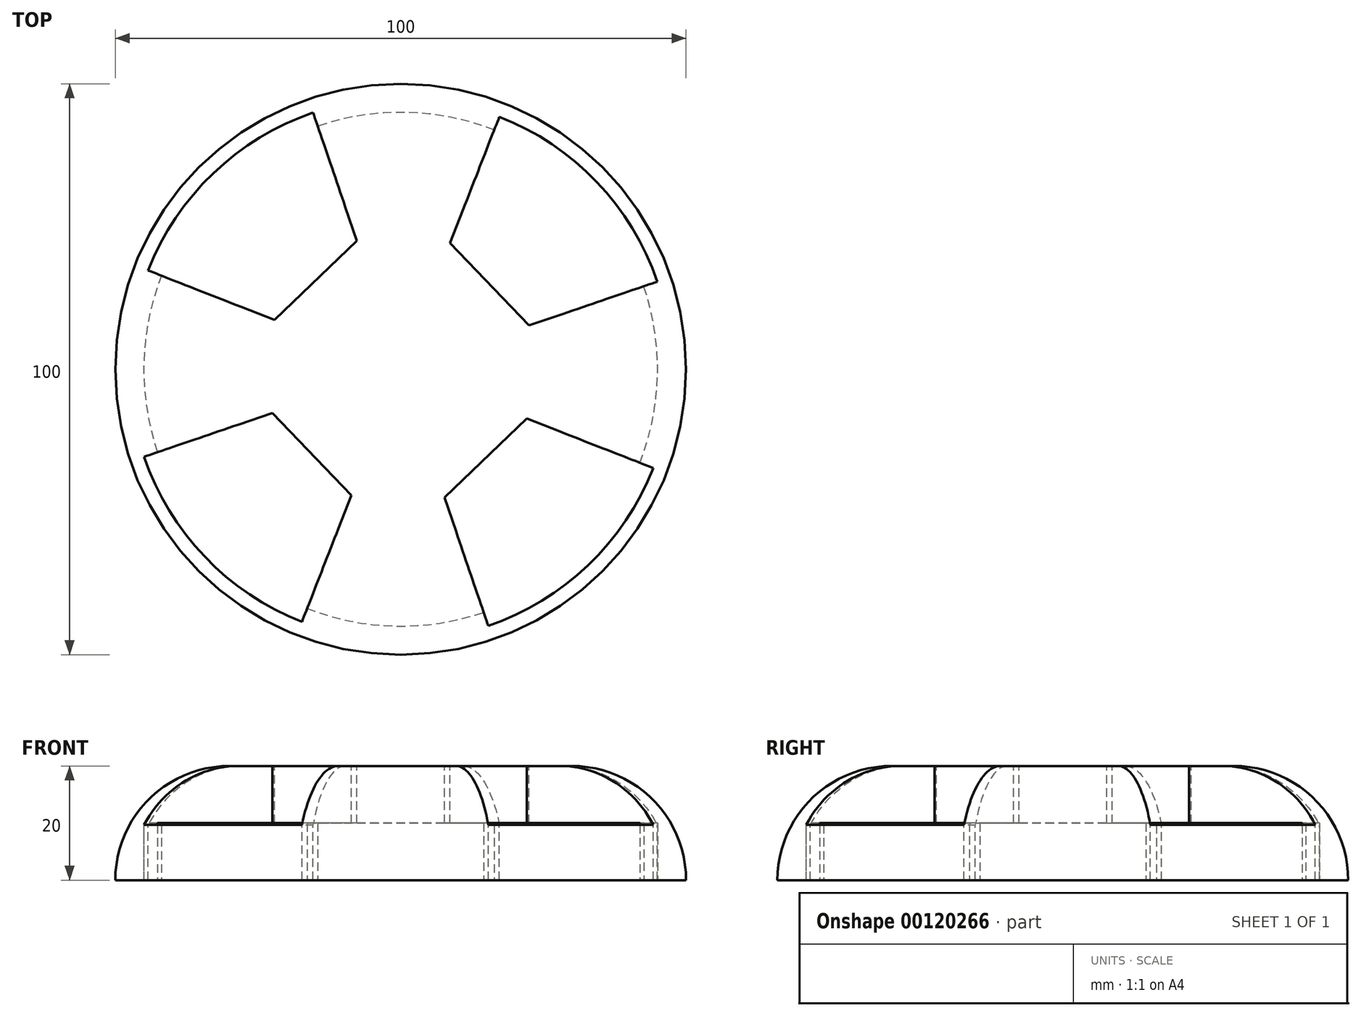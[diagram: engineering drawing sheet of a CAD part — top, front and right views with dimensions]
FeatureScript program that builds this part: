
annotation { "Feature Type Name" : "Feature", "Feature Type Description" : "" }
export const myFeature = defineFeature(function(context is Context, id is Id, definition is map)
    precondition{}
    {
        {
            var Q0;
            Q0=qCreatedBy(makeId("Top.planeOp"),FACE);
            var sketch = newSketch(context, id + "F0", { "sketchPlane" : qUnion([Q0])});
            skCircle(sketch, "E0", {"center": v(0, 0) * mm, "radius": 50 * mm});
            skSolve(sketch);
        }
        {
            var Q0;
            Q0 = qSketchRegion(id + "F0", true);
            extrude(context, id + "F1", {"entities" : qUnion([Q0]), "depth" : 20 * mm, "offsetDistance" : 25 * mm});
        }
        {
            var Q0;
            Q0=makeQuery(id+"F1.opExtrude","CAP_EDGE",EDGE,{"disambiguationData":[OSD([sQuery(id+"F0.wireOp",EDGE,"E0")])],"isStart":false});
            fillet(context, id + "F2", {"entities" : qUnion([Q0]), "radius" : 20 * mm, "tangentPropagation" : true, "allowEdgeOverflow" : false});
        }
        {
            var Q0;
            Q0=makeQuery(id+"F1.opExtrude","CAP_FACE",FACE,{"disambiguationData":[OSD([sQuery(id+"F0.wireOp",EDGE,"E0")])],"isStart":true});
            var sketch = newSketch(context, id + "F3", { "sketchPlane" : qUnion([Q0])});
            skCircle(sketch, "E1", {"center": v(0, 0) * mm, "radius": 45 * mm});
            skSolve(sketch);
        }
        {
            var Q0;
            Q0 = qSketchRegion(id + "F3", true);
            extrude(context, id + "F4", {"entities" : qUnion([Q0]), "operationType" : NewBodyOperationType.REMOVE, "oppositeDirection" : true, "depth" : 10 * mm, "offsetDistance" : 25 * mm});
        }
        {
            var Q0;
            Q0=makeQuery(id+"F1.opExtrude","CAP_FACE",FACE,{"disambiguationData":[OSD([sQuery(id+"F0.wireOp",EDGE,"E0")])],"isStart":false});
            var sketch = newSketch(context, id + "F5", { "sketchPlane" : qUnion([Q0])});
            skLineSegment(sketch, "E2.bottom", {"start": v(-61.82, 35.67) * mm, "end": v(-32.92, 63.33) * mm, "construction": true});
            skLineSegment(sketch, "E2.top", {"start": v(-44.24, 17.3) * mm, "end": v(-15.34, 44.96) * mm, "construction": true});
            skLineSegment(sketch, "E2.left", {"start": v(-61.82, 35.67) * mm, "end": v(-44.24, 17.3) * mm, "construction": true});
            skLineSegment(sketch, "E2.right", {"start": v(-32.92, 63.33) * mm, "end": v(-15.34, 44.96) * mm, "construction": true});
            skLineSegment(sketch, "E3.bottom", {"start": v(35.67, 61.82) * mm, "end": v(63.33, 32.92) * mm, "construction": true});
            skLineSegment(sketch, "E3.top", {"start": v(17.3, 44.24) * mm, "end": v(44.96, 15.34) * mm, "construction": true});
            skLineSegment(sketch, "E3.left", {"start": v(35.67, 61.82) * mm, "end": v(17.3, 44.24) * mm, "construction": true});
            skLineSegment(sketch, "E3.right", {"start": v(63.33, 32.92) * mm, "end": v(44.96, 15.34) * mm, "construction": true});
            skLineSegment(sketch, "E4.bottom", {"start": v(-44.96, -15.34) * mm, "end": v(-17.3, -44.24) * mm, "construction": true});
            skLineSegment(sketch, "E4.top", {"start": v(-63.33, -32.92) * mm, "end": v(-35.67, -61.82) * mm, "construction": true});
            skLineSegment(sketch, "E4.left", {"start": v(-44.96, -15.34) * mm, "end": v(-63.33, -32.92) * mm, "construction": true});
            skLineSegment(sketch, "E4.right", {"start": v(-17.3, -44.24) * mm, "end": v(-35.67, -61.82) * mm, "construction": true});
            skLineSegment(sketch, "E5.bottom", {"start": v(15.34, -44.96) * mm, "end": v(44.24, -17.3) * mm, "construction": true});
            skLineSegment(sketch, "E5.top", {"start": v(32.92, -63.33) * mm, "end": v(61.82, -35.67) * mm, "construction": true});
            skLineSegment(sketch, "E5.left", {"start": v(15.34, -44.96) * mm, "end": v(32.92, -63.33) * mm, "construction": true});
            skLineSegment(sketch, "E5.right", {"start": v(44.24, -17.3) * mm, "end": v(61.82, -35.67) * mm, "construction": true});
            skCircle(sketch, "E6", {"center": v(0, 0) * mm, "radius": 47.5 * mm, "construction": true});
            skArc(sketch, "E7", {"start": v(-44.96, -15.34) * mm, "mid": v(-34.32, -32.84) * mm, "end": v(-17.3, -44.24) * mm});
            skLineSegment(sketch, "E8", {"start": v(-44.96, -15.34) * mm, "end": v(-22.48, -7.67) * mm});
            skLineSegment(sketch, "E9", {"start": v(-8.65, -22.12) * mm, "end": v(-17.3, -44.24) * mm});
            skArc(sketch, "E10", {"start": v(-15.34, 44.96) * mm, "mid": v(-32.84, 34.32) * mm, "end": v(-44.24, 17.3) * mm});
            skArc(sketch, "E11", {"start": v(44.96, 15.34) * mm, "mid": v(34.32, 32.84) * mm, "end": v(17.3, 44.24) * mm});
            skArc(sketch, "E12", {"start": v(15.34, -44.96) * mm, "mid": v(32.84, -34.32) * mm, "end": v(44.24, -17.3) * mm});
            skLineSegment(sketch, "E13", {"start": v(-44.24, 17.3) * mm, "end": v(-22.12, 8.65) * mm});
            skLineSegment(sketch, "E14", {"start": v(-15.34, 44.96) * mm, "end": v(-7.67, 22.48) * mm});
            skLineSegment(sketch, "E15", {"start": v(17.3, 44.24) * mm, "end": v(8.65, 22.12) * mm});
            skLineSegment(sketch, "E16", {"start": v(44.96, 15.34) * mm, "end": v(22.48, 7.67) * mm});
            skLineSegment(sketch, "E17", {"start": v(15.34, -44.96) * mm, "end": v(7.67, -22.48) * mm});
            skLineSegment(sketch, "E18", {"start": v(44.24, -17.3) * mm, "end": v(22.12, -8.65) * mm});
            skLineSegment(sketch, "E19", {"start": v(-22.48, -7.67) * mm, "end": v(-8.65, -22.12) * mm});
            skLineSegment(sketch, "E20", {"start": v(-22.12, 8.65) * mm, "end": v(-7.67, 22.48) * mm});
            skLineSegment(sketch, "E21", {"start": v(8.65, 22.12) * mm, "end": v(22.48, 7.67) * mm});
            skLineSegment(sketch, "E22", {"start": v(7.67, -22.48) * mm, "end": v(22.12, -8.65) * mm});
            skSolve(sketch);
        }
        {
            var Q0;
            Q0 = qSketchRegion(id + "F5", true);
            extrude(context, id + "F6", {"entities" : qUnion([Q0]), "operationType" : NewBodyOperationType.REMOVE, "oppositeDirection" : true, "depth" : 25 * mm, "offsetDistance" : 25 * mm});
        }
    });
